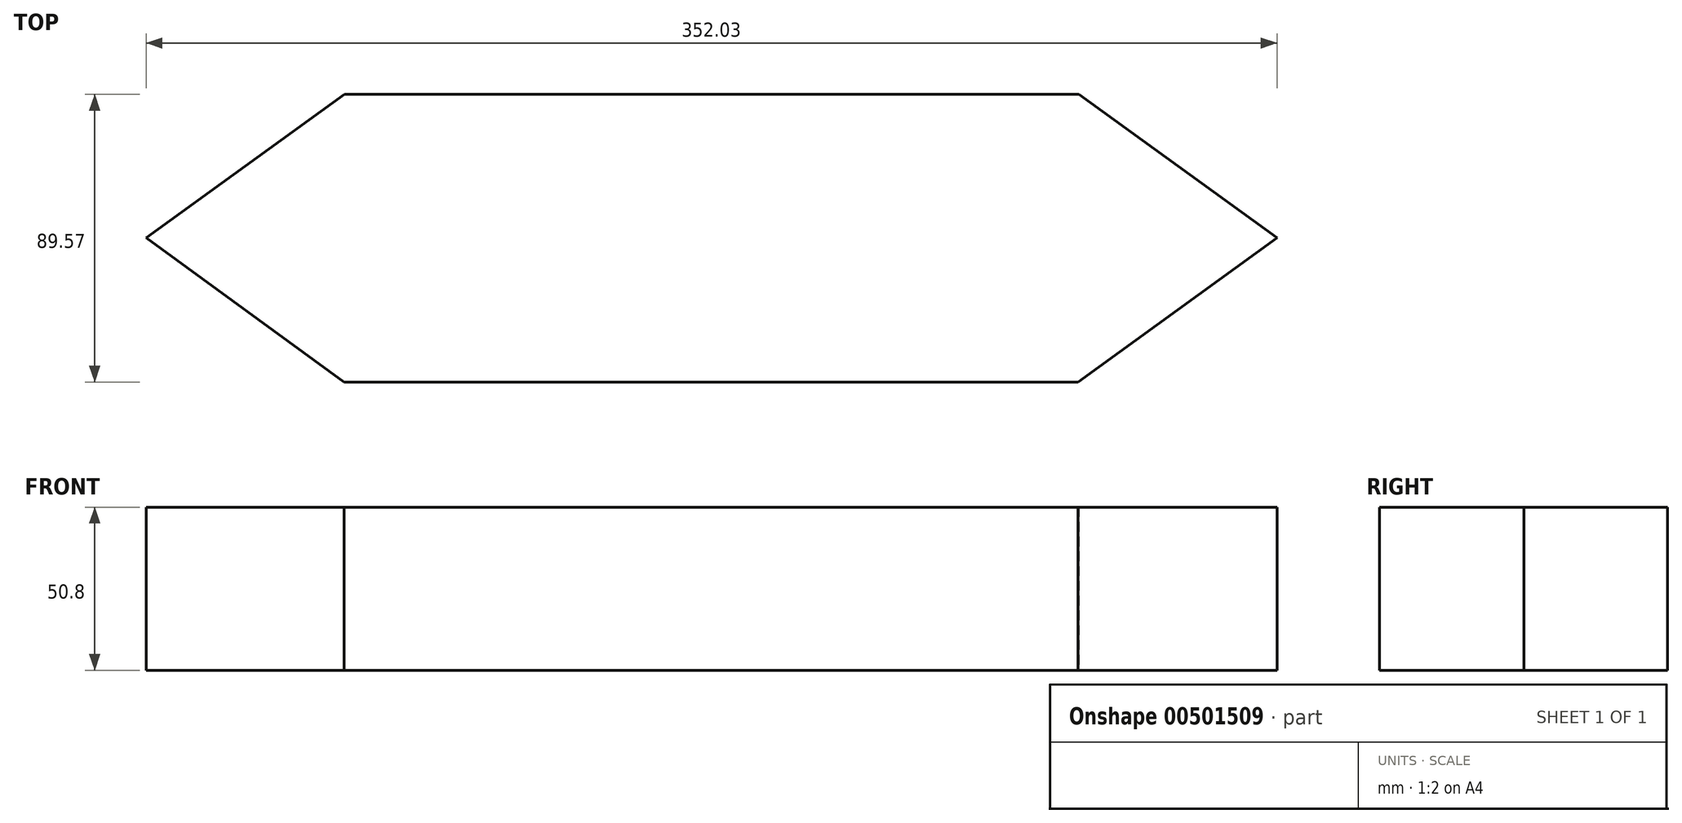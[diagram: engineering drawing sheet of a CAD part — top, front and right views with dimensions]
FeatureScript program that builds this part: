
annotation { "Feature Type Name" : "Feature", "Feature Type Description" : "" }
export const myFeature = defineFeature(function(context is Context, id is Id, definition is map)
    precondition{}
    {
        {
            var Q0;
            Q0=qCreatedBy(makeId("Top.planeOp"),FACE);
            var sketch = newSketch(context, id + "F0", { "sketchPlane" : qUnion([Q0])});
            skLineSegment(sketch, "E0", {"start": v(0, 0) * mm, "end": v(61.58, -44.88) * mm});
            skLineSegment(sketch, "E1", {"start": v(0, 0) * mm, "end": v(61.72, 44.7) * mm});
            skLineSegment(sketch, "E2", {"start": v(61.72, 44.7) * mm, "end": v(290.32, 44.7) * mm});
            skLineSegment(sketch, "E3", {"start": v(61.58, -44.88) * mm, "end": v(290.18, -44.88) * mm});
            skLineSegment(sketch, "E4", {"start": v(290.32, 44.7) * mm, "end": v(352.03, 0) * mm});
            skLineSegment(sketch, "E5", {"start": v(290.18, -44.88) * mm, "end": v(352.03, 0) * mm});
            skSolve(sketch);
        }
        {
            var Q0;
            Q0 = qSketchRegion(id + "F0", true);
            extrude(context, id + "F1", {"entities" : qUnion([Q0]), "depth" : 50.8 * mm});
        }
    });
